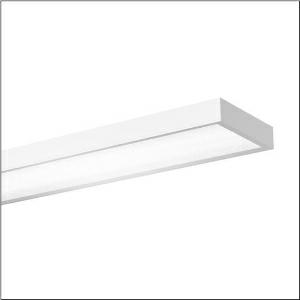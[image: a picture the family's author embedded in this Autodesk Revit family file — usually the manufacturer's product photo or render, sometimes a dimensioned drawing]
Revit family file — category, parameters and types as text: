
# Revit family: sport_31_51hs12dd4gca
name_source: partatom
category: Lighting Fixtures
units: mm (PartAtom-declared; Revit-internal decimal feet)

## family parameters
Cut with Voids When Loaded = No
Host = Face
Light Source = No
Part Type = Normal
Room Calculation Point = No
Round Connector Dimension = Use Diameter
Shared = No

## types (1)
- --- (1 x LED, 15290 lm, 113 W, 4000K)
    Apparent Load = 113 VA
    CIE Flux Codes = 65 89 97 100 100
    Color Rendering = 80
    Color Temperature = 4000K
    Default Elevation = 1800 mm
    Description = Sport 31, LED high bay luminaire, primary light control with reflector, of sheet steel, primary anti-glare with prismatic structure, of PC, primary optical cover: cover panel, of PC, light emission: direct distribution, primary light characteristic: symmetric, installation type: suspended mounting, recessed, surface-mounted, LED, rated luminous flux: 16.000lm, luminous efficacy: 137lm/W, light colour: 840, colour temperature: 4000K, control gear: ECG DALI, with terminal, 5-pole, max. 2.5mm², mains connection: 220..240V, AC, 50/60Hz, rated input power: 117W, housing, of sheet steel, traffic white (RAL 9016), length: 1.540mm, width: 415mm, height: 95mm, protection rating (complete): IP20, protection rating (lamp compartment, on room side): IP50, insulation class (complete): insulation class I (protective earthing), certification: CE, ENEC, UKCA, ball protection: ball impact resistant with ceiling mounting or chain suspension, impact resistance: IK08, permissible operating ambient temperature: -20..+35°C, standard: DIN 18032-3, packaging unit: 1 piece
    Height = 100 mm  [stored 0.328084 ft]
    Lamp = 1 x LED
    Lamp Light Flux = 15290 lm
    Lamp Power = 113 W
    Lamp count = 1
    Length = 1500 mm
    Luminous efficacy = 135 lm/W
    Manufacturer = Siteco
    ModVariant = No
    Model = 51HS12DD4GCA
    Mounting Place = Ceiling
    Mounting Type = Pendant
    Number of Poles = 1
    OnlyDefault = Yes
    Power Factor = 1
    Product Name = Sport 31
    Product group = LED high bay luminaire
    ProductGroupID = 903
    Protection Class = Protection class I
    Protection Degree = IP 20
    RLX_Detail_Level = 1
    RlxData = <blob elided: 24037 chars, md5=d3187064>
    Socket = socket
    Standby Power = 0 W
    System Light Flux = 15290 lm
    System Power = 113 W
    Type Comments = factory setting: luminous flux: 100 % | dim-lin: 254 | 558 mA
    Type Image = l_1006829.jpg
    URL = http://relux.com
    VarID = @adj_121061
    Voltage = 0 V
    Weight = 0.00 kg
    Width = 415 mm

note: [stored X ft] marks values corroborated as IEEE doubles in the binary element streams (Revit-internal decimal feet)

## geometry (parser evidence)
native form markers: Blend x4, Sweep x12
no freeform markers — native parametric forms only
